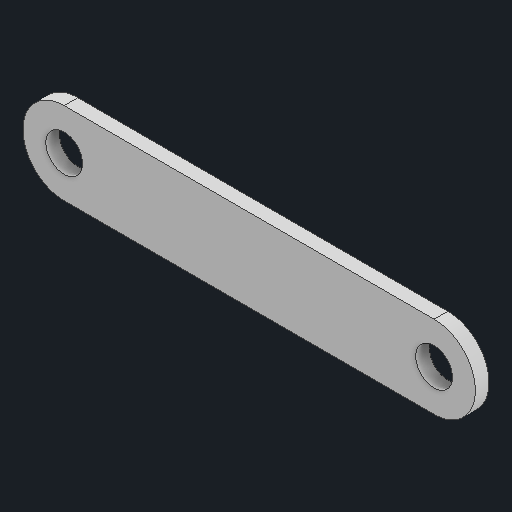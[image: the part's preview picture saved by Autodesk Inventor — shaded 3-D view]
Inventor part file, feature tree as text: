
AUTODESK INVENTOR PART (.ipt)
format: ipt  version: 2025 (Build 290162000, 162)  size: 93,184 bytes
history: native  units: in
note: dims shown in document units (in); Inventor stores cm internally (conversion verified against a paired STEP export)
features: extrude x1, sketch x1
ambient origin geometry x8: Origin, YZ Plane, XZ Plane, XY Plane, X Axis, Y Axis, Z Axis, Center Point
bodies: Solid1 (feature_tree)
feature tree (2):
  extrude  "Extrusion1"  Depth=0.0625in
  sketch  "Sketch1"  dims[d0=0.167in d1=0.167in d2=0.0625in d3=0.0in]
